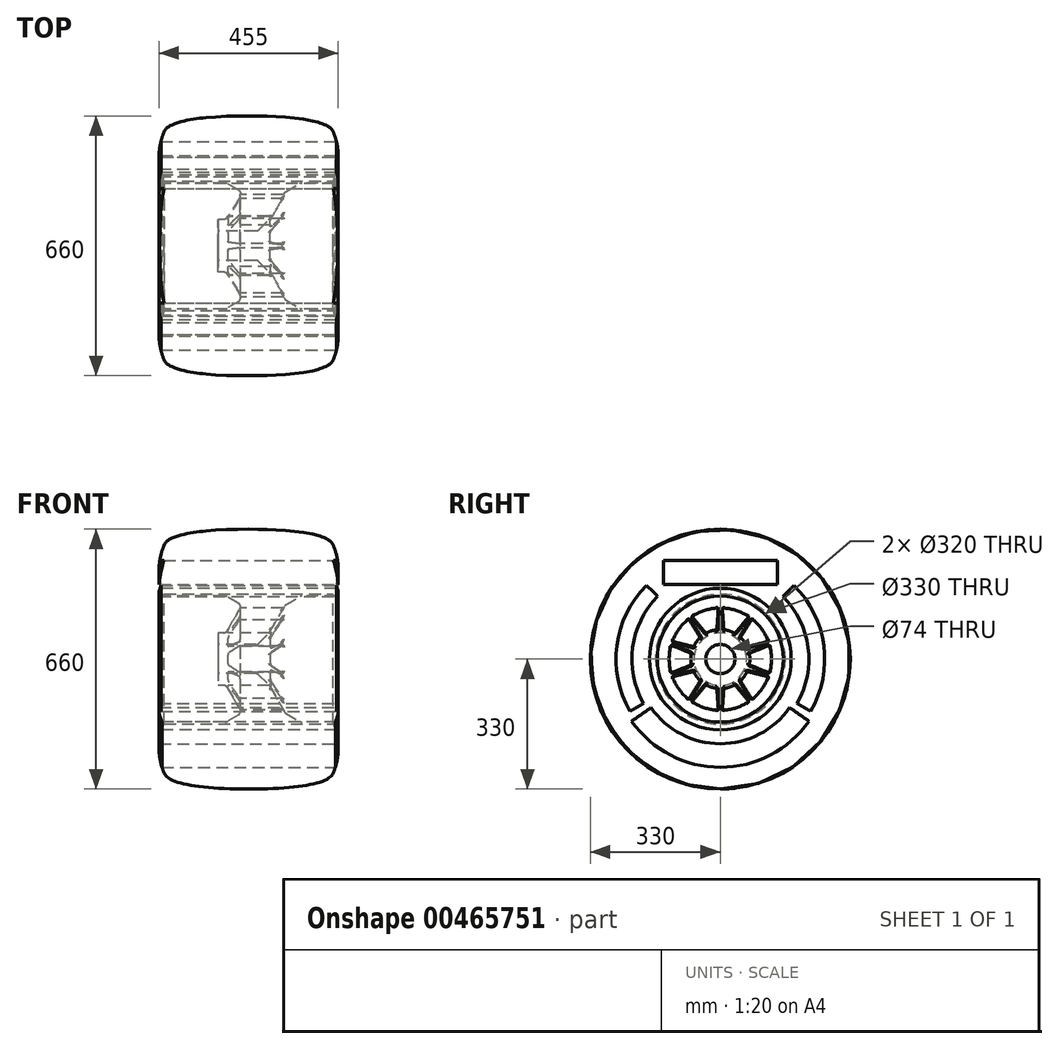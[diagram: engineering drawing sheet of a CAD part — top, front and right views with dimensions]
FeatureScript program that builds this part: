
annotation { "Feature Type Name" : "Feature", "Feature Type Description" : "" }
export const myFeature = defineFeature(function(context is Context, id is Id, definition is map)
    precondition{}
    {
        {
            var Q0;
            Q0=qCreatedBy(makeId("Front.planeOp"),FACE);
            var sketch = newSketch(context, id + "F0", { "sketchPlane" : qUnion([Q0])});
            skLineSegment(sketch, "E0.bottom", {"start": v(0, 0) * mm, "end": v(-232.5, 0) * mm, "construction": true});
            skLineSegment(sketch, "E0.top", {"start": v(0, 340) * mm, "end": v(-232.5, 340) * mm, "construction": true});
            skLineSegment(sketch, "E0.left", {"start": v(0, 0) * mm, "end": v(0, 340) * mm, "construction": true});
            skLineSegment(sketch, "E0.right", {"start": v(-232.5, 0) * mm, "end": v(-232.5, 340) * mm, "construction": true});
            skLineSegment(sketch, "E1", {"start": v(0, 165) * mm, "end": v(-214.65, 165) * mm});
            skEllipticalArc(sketch, "E2", {});
            skLineSegment(sketch, "E3", {"start": v(0, 330) * mm, "end": v(-232.5, 330) * mm, "construction": true});
            skLineSegment(sketch, "E4", {"start": v(-214.65, 165) * mm, "end": v(-214.65, 290) * mm, "construction": true});
            skEllipticalArc(sketch, "E5", {});
            skLineSegment(sketch, "E6", {"start": v(-227.5, 227.5) * mm, "end": v(-214.65, 227.5) * mm, "construction": true});
            skLineSegment(sketch, "E7.MirrorCS", {"start": v(0, 165) * mm, "end": v(214.65, 165) * mm});
            skEllipticalArc(sketch, "E8.MirrorCS", {});
            skEllipticalArc(sketch, "E9.MirrorCS", {});
            skLineSegment(sketch, "E10", {"start": v(-227.5, 227.5) * mm, "end": v(-227.5, 0) * mm, "construction": true});
            skLineSegment(sketch, "E11.MirrorCS", {"start": v(232.5, 0) * mm, "end": v(232.5, 340) * mm, "construction": true});
            skLineSegment(sketch, "E12.MirrorCS", {"start": v(0, 340) * mm, "end": v(232.5, 340) * mm, "construction": true});
            skLineSegment(sketch, "E13.MirrorCS", {"start": v(0, 0) * mm, "end": v(232.5, 0) * mm, "construction": true});
            const initialGuessF0  = {"E2": [0.9663548736200733, 0.07278752318222956, 0.9840924206940259, -0.17765727548449584, 1.201246100909484, 0.14589798289999634, 2.549372753708736, 3.1145633278998273], "E5": [0.08535, 0.2275, -1, 0, 0.31285, 0.22033704343395144, 5.995580380133269, 0.28760492704630874], "E8.MirrorCS": [-0.08535, 0.2275, 1, 0, 0.31285, 0.22033704343395144, 5.995580380133277, 0.28760492704631696], "E9.MirrorCS": [-0.9663548736200733, 0.07278752318222961, -0.984092420694026, -0.17765727548449584, 1.201246100909484, 0.14589798289999634, 3.168621979279758, 3.733812553470848]};
            skSetInitialGuess(sketch, initialGuessF0);
            skSolve(sketch);
        }
        {
            var Q0;
            Q0=qCreatedBy(makeId("Right.planeOp"),FACE);
            var sketch = newSketch(context, id + "F1", { "sketchPlane" : qUnion([Q0])});
            skLineSegment(sketch, "E14", {"start": v(0, 190) * mm, "end": v(0, -215) * mm, "construction": true});
            skLineSegment(sketch, "E15.bottom", {"start": v(0, 190) * mm, "end": v(-145, 190) * mm});
            skLineSegment(sketch, "E15.top", {"start": v(0, 250) * mm, "end": v(-145, 250) * mm});
            skLineSegment(sketch, "E15.left", {"start": v(0, 190) * mm, "end": v(0, 250) * mm});
            skLineSegment(sketch, "E15.right", {"start": v(-145, 190) * mm, "end": v(-145, 250) * mm});
            skArc(sketch, "E16", {"start": v(-159.1, 159.1) * mm, "mid": v(-223.08, 29.37) * mm, "end": v(-194.86, -112.5) * mm});
            skArc(sketch, "E17", {"start": v(-187.38, 187.38) * mm, "mid": v(-262.73, 34.59) * mm, "end": v(-229.5, -132.5) * mm});
            skLineSegment(sketch, "E18", {"start": v(-159.1, 159.1) * mm, "end": v(-187.38, 187.38) * mm});
            skLineSegment(sketch, "E19", {"start": v(-194.86, -112.5) * mm, "end": v(-229.5, -132.5) * mm});
            skArc(sketch, "E20", {"start": v(-176.12, -123.32) * mm, "mid": v(-99.28, -190.7) * mm, "end": v(0, -215) * mm});
            skArc(sketch, "E21", {"start": v(-225.27, -157.73) * mm, "mid": v(-126.98, -243.93) * mm, "end": v(0, -275) * mm});
            skLineSegment(sketch, "E22", {"start": v(-176.12, -123.32) * mm, "end": v(-225.27, -157.73) * mm});
            skLineSegment(sketch, "E23", {"start": v(0, -215) * mm, "end": v(0, -275) * mm});
            skLineSegment(sketch, "E24.MirrorCS", {"start": v(0, 250) * mm, "end": v(145, 250) * mm});
            skLineSegment(sketch, "E25.MirrorCS", {"start": v(145, 190) * mm, "end": v(145, 250) * mm});
            skLineSegment(sketch, "E26.MirrorCS", {"start": v(0, 190) * mm, "end": v(145, 190) * mm});
            skLineSegment(sketch, "E27.MirrorCS", {"start": v(159.1, 159.1) * mm, "end": v(187.38, 187.38) * mm});
            skArc(sketch, "E28.MirrorCS", {"start": v(187.38, 187.38) * mm, "mid": v(262.73, 34.59) * mm, "end": v(229.5, -132.5) * mm});
            skArc(sketch, "E29.MirrorCS", {"start": v(159.1, 159.1) * mm, "mid": v(223.08, 29.37) * mm, "end": v(194.86, -112.5) * mm});
            skLineSegment(sketch, "E30.MirrorCS", {"start": v(194.86, -112.5) * mm, "end": v(229.5, -132.5) * mm});
            skLineSegment(sketch, "E31.MirrorCS", {"start": v(176.12, -123.32) * mm, "end": v(225.27, -157.73) * mm});
            skArc(sketch, "E32.MirrorCS", {"start": v(225.27, -157.73) * mm, "mid": v(126.98, -243.93) * mm, "end": v(0, -275) * mm});
            skArc(sketch, "E33.MirrorCS", {"start": v(176.12, -123.32) * mm, "mid": v(99.28, -190.7) * mm, "end": v(0, -215) * mm});
            skSolve(sketch);
        }
        {
            var Q0;
            Q0=qCreatedBy(makeId("Front.planeOp"),FACE);
            var sketch = newSketch(context, id + "F2", { "sketchPlane" : qUnion([Q0])});
            skLineSegment(sketch, "E34.bottom", {"start": v(-222.5, 180) * mm, "end": v(222.5, 180) * mm});
            skLineSegment(sketch, "E34.top", {"start": v(-222.5, 160) * mm, "end": v(-60.18, 160) * mm});
            skLineSegment(sketch, "E34.left", {"start": v(-227.5, 175) * mm, "end": v(-227.5, 165) * mm});
            skLineSegment(sketch, "E34.right", {"start": v(227.5, 175) * mm, "end": v(227.5, 165) * mm});
            skPoint(sketch, "E35.visualSharp", {"position": v(-227.5, 160) * mm});
            skArc(sketch, "E35.filletArc", {"start": v(-227.5, 165) * mm, "mid": v(-226.04, 161.46) * mm, "end": v(-222.5, 160) * mm});
            skPoint(sketch, "E36.visualSharp", {"position": v(227.5, 160) * mm});
            skArc(sketch, "E36.filletArc", {"start": v(222.5, 160) * mm, "mid": v(226.04, 161.46) * mm, "end": v(227.5, 165) * mm});
            skPoint(sketch, "E37.visualSharp", {"position": v(227.5, 180) * mm});
            skArc(sketch, "E37.filletArc", {"start": v(227.5, 175) * mm, "mid": v(226.04, 178.54) * mm, "end": v(222.5, 180) * mm});
            skPoint(sketch, "E38.visualSharp", {"position": v(-227.5, 180) * mm});
            skArc(sketch, "E38.filletArc", {"start": v(-222.5, 180) * mm, "mid": v(-226.04, 178.54) * mm, "end": v(-227.5, 175) * mm});
            skLineSegment(sketch, "E39", {"start": v(18.36, 37) * mm, "end": v(-77.5, 37) * mm});
            skLineSegment(sketch, "E40", {"start": v(-77.5, 37) * mm, "end": v(-77.5, 67) * mm});
            skLineSegment(sketch, "E41", {"start": v(-77.5, 67) * mm, "end": v(-63.27, 67) * mm});
            skLineSegment(sketch, "E42", {"start": v(-54.61, 72) * mm, "end": v(-22.23, 128.09) * mm});
            skLineSegment(sketch, "E43", {"start": v(-25.9, 141.75) * mm, "end": v(-55.18, 158.66) * mm});
            skLineSegment(sketch, "E44", {"start": v(25.43, 39.93) * mm, "end": v(51.57, 66.07) * mm});
            skLineSegment(sketch, "E45", {"start": v(53.16, 68.14) * mm, "end": v(91.43, 134.43) * mm});
            skLineSegment(sketch, "E46", {"start": v(95.1, 138.09) * mm, "end": v(130.72, 158.66) * mm});
            skLineSegment(sketch, "E47.trimOffspring", {"start": v(135.72, 160) * mm, "end": v(222.5, 160) * mm});
            skPoint(sketch, "E48.visualSharp", {"position": v(-57.5, 160) * mm});
            skArc(sketch, "E48.filletArc", {"start": v(-55.18, 158.66) * mm, "mid": v(-57.6, 159.66) * mm, "end": v(-60.18, 160) * mm});
            skPoint(sketch, "E49.visualSharp", {"position": v(-57.5, 67) * mm});
            skArc(sketch, "E49.filletArc", {"start": v(-63.27, 67) * mm, "mid": v(-58.27, 68.34) * mm, "end": v(-54.61, 72) * mm});
            skPoint(sketch, "E50.visualSharp", {"position": v(22.5, 37) * mm});
            skArc(sketch, "E50.filletArc", {"start": v(18.36, 37) * mm, "mid": v(22.18, 37.76) * mm, "end": v(25.43, 39.93) * mm});
            skPoint(sketch, "E51.visualSharp", {"position": v(52.5, 67) * mm});
            skArc(sketch, "E51.filletArc", {"start": v(51.57, 66.07) * mm, "mid": v(52.43, 67.05) * mm, "end": v(53.16, 68.14) * mm});
            skPoint(sketch, "E52.visualSharp", {"position": v(92.77, 136.75) * mm});
            skPoint(sketch, "E53.visualSharp", {"position": v(133.04, 160) * mm});
            skArc(sketch, "E53.filletArc", {"start": v(135.72, 160) * mm, "mid": v(133.13, 159.66) * mm, "end": v(130.72, 158.66) * mm});
            skPoint(sketch, "E54.visualSharp", {"position": v(-17.23, 136.75) * mm});
            skArc(sketch, "E54.filletArc", {"start": v(-22.23, 128.09) * mm, "mid": v(-21.23, 135.68) * mm, "end": v(-25.9, 141.75) * mm});
            skArc(sketch, "E55.filletArc", {"start": v(95.1, 138.09) * mm, "mid": v(93.02, 136.5) * mm, "end": v(91.43, 134.43) * mm});
            skSolve(sketch);
        }
        {
            var Q0;
            Q0=qCreatedBy(makeId("Right.planeOp"),FACE);
            var sketch = newSketch(context, id + "F3", { "sketchPlane" : qUnion([Q0])});
            skLineSegment(sketch, "E56", {"start": v(5.4, 124.22) * mm, "end": v(8.6, 78.49) * mm});
            skLineSegment(sketch, "E57", {"start": v(40.17, 123.64) * mm, "end": v(23.18, 71.33) * mm, "construction": true});
            skLineSegment(sketch, "E58", {"start": v(23.18, 71.33) * mm, "end": v(0, 0) * mm, "construction": true});
            skArc(sketch, "E59", {"start": v(23.18, 71.33) * mm, "mid": v(18, 72.8) * mm, "end": v(12.73, 73.91) * mm});
            skArc(sketch, "E60", {"start": v(40.17, 123.64) * mm, "mid": v(25.66, 127.44) * mm, "end": v(10.8, 129.55) * mm});
            skArc(sketch, "E61.MirrorCS", {"start": v(23.18, 71.33) * mm, "mid": v(28.23, 69.48) * mm, "end": v(33.14, 67.28) * mm});
            skLineSegment(sketch, "E62.MirrorCS", {"start": v(68.65, 103.67) * mm, "end": v(39.18, 68.55) * mm});
            skArc(sketch, "E63.MirrorCS", {"start": v(40.17, 123.64) * mm, "mid": v(54.15, 118.18) * mm, "end": v(67.4, 111.16) * mm});
            skPoint(sketch, "E64.visualSharp", {"position": v(8.88, 74.47) * mm});
            skArc(sketch, "E64.filletArc", {"start": v(8.6, 78.49) * mm, "mid": v(9.87, 75.49) * mm, "end": v(12.73, 73.91) * mm});
            skPoint(sketch, "E65.visualSharp", {"position": v(5, 129.9) * mm});
            skArc(sketch, "E65.filletArc", {"start": v(10.8, 129.55) * mm, "mid": v(6.87, 128.13) * mm, "end": v(5.4, 124.22) * mm});
            skPoint(sketch, "E66.visualSharp", {"position": v(36.6, 65.47) * mm});
            skArc(sketch, "E66.filletArc", {"start": v(33.14, 67.28) * mm, "mid": v(36.38, 66.87) * mm, "end": v(39.18, 68.55) * mm});
            skPoint(sketch, "E67.visualSharp", {"position": v(72.31, 108.03) * mm});
            skArc(sketch, "E67.filletArc", {"start": v(68.65, 103.67) * mm, "mid": v(69.75, 107.7) * mm, "end": v(67.4, 111.16) * mm});
            skLineSegment(sketch, "E68.1.0", {"start": v(-5.4, 124.22) * mm, "end": v(-8.6, 78.49) * mm});
            skArc(sketch, "E68.1.1", {"start": v(-5.4, 124.22) * mm, "mid": v(-6.87, 128.13) * mm, "end": v(-10.8, 129.55) * mm});
            skArc(sketch, "E68.1.2", {"start": v(-40.17, 123.64) * mm, "mid": v(-25.66, 127.44) * mm, "end": v(-10.8, 129.55) * mm});
            skArc(sketch, "E68.1.3", {"start": v(-40.17, 123.64) * mm, "mid": v(-54.15, 118.18) * mm, "end": v(-67.4, 111.16) * mm});
            skArc(sketch, "E68.1.4", {"start": v(-67.4, 111.16) * mm, "mid": v(-69.75, 107.7) * mm, "end": v(-68.65, 103.67) * mm});
            skLineSegment(sketch, "E68.1.5", {"start": v(-68.65, 103.67) * mm, "end": v(-39.18, 68.55) * mm});
            skArc(sketch, "E68.1.6", {"start": v(-39.18, 68.55) * mm, "mid": v(-36.38, 66.87) * mm, "end": v(-33.14, 67.28) * mm});
            skArc(sketch, "E68.1.7", {"start": v(-23.18, 71.33) * mm, "mid": v(-28.23, 69.48) * mm, "end": v(-33.14, 67.28) * mm});
            skArc(sketch, "E68.1.8", {"start": v(-23.18, 71.33) * mm, "mid": v(-18, 72.8) * mm, "end": v(-12.73, 73.91) * mm});
            skArc(sketch, "E68.1.9", {"start": v(-12.73, 73.91) * mm, "mid": v(-9.87, 75.49) * mm, "end": v(-8.6, 78.49) * mm});
            skLineSegment(sketch, "E68.2.0", {"start": v(-77.38, 97.32) * mm, "end": v(-53.09, 58.45) * mm});
            skArc(sketch, "E68.2.1", {"start": v(-77.38, 97.32) * mm, "mid": v(-80.87, 99.62) * mm, "end": v(-84.89, 98.46) * mm});
            skArc(sketch, "E68.2.2", {"start": v(-105.17, 76.41) * mm, "mid": v(-95.67, 88.02) * mm, "end": v(-84.89, 98.46) * mm});
            skArc(sketch, "E68.2.3", {"start": v(-105.17, 76.41) * mm, "mid": v(-113.28, 63.78) * mm, "end": v(-119.87, 50.3) * mm});
            skArc(sketch, "E68.2.4", {"start": v(-119.87, 50.3) * mm, "mid": v(-119.73, 46.13) * mm, "end": v(-116.47, 43.52) * mm});
            skLineSegment(sketch, "E68.2.5", {"start": v(-116.47, 43.52) * mm, "end": v(-72, 32.43) * mm});
            skArc(sketch, "E68.2.6", {"start": v(-72, 32.43) * mm, "mid": v(-68.74, 32.72) * mm, "end": v(-66.36, 34.95) * mm});
            skArc(sketch, "E68.2.7", {"start": v(-60.68, 44.08) * mm, "mid": v(-63.68, 39.62) * mm, "end": v(-66.36, 34.95) * mm});
            skArc(sketch, "E68.2.8", {"start": v(-60.68, 44.08) * mm, "mid": v(-57.36, 48.32) * mm, "end": v(-53.75, 52.31) * mm});
            skArc(sketch, "E68.2.9", {"start": v(-53.75, 52.31) * mm, "mid": v(-52.36, 55.27) * mm, "end": v(-53.09, 58.45) * mm});
            skLineSegment(sketch, "E68.3.0", {"start": v(-119.8, 33.25) * mm, "end": v(-77.3, 16.08) * mm});
            skArc(sketch, "E68.3.1", {"start": v(-119.8, 33.25) * mm, "mid": v(-123.98, 33.06) * mm, "end": v(-126.55, 29.76) * mm});
            skArc(sketch, "E68.3.2", {"start": v(-130, 0) * mm, "mid": v(-129.13, 14.98) * mm, "end": v(-126.55, 29.76) * mm});
            skArc(sketch, "E68.3.3", {"start": v(-130, 0) * mm, "mid": v(-129.13, -14.98) * mm, "end": v(-126.55, -29.76) * mm});
            skArc(sketch, "E68.3.4", {"start": v(-126.55, -29.76) * mm, "mid": v(-123.98, -33.06) * mm, "end": v(-119.8, -33.25) * mm});
            skLineSegment(sketch, "E68.3.5", {"start": v(-119.8, -33.25) * mm, "end": v(-77.3, -16.08) * mm});
            skArc(sketch, "E68.3.6", {"start": v(-77.3, -16.08) * mm, "mid": v(-74.84, -13.94) * mm, "end": v(-74.23, -10.73) * mm});
            skArc(sketch, "E68.3.7", {"start": v(-75, 0) * mm, "mid": v(-74.8, -5.38) * mm, "end": v(-74.23, -10.73) * mm});
            skArc(sketch, "E68.3.8", {"start": v(-75, 0) * mm, "mid": v(-74.8, 5.38) * mm, "end": v(-74.23, 10.73) * mm});
            skArc(sketch, "E68.3.9", {"start": v(-74.23, 10.73) * mm, "mid": v(-74.84, 13.94) * mm, "end": v(-77.3, 16.08) * mm});
            skLineSegment(sketch, "E68.4.0", {"start": v(-116.47, -43.52) * mm, "end": v(-72, -32.43) * mm});
            skArc(sketch, "E68.4.1", {"start": v(-116.47, -43.52) * mm, "mid": v(-119.73, -46.13) * mm, "end": v(-119.87, -50.3) * mm});
            skArc(sketch, "E68.4.2", {"start": v(-105.17, -76.41) * mm, "mid": v(-113.28, -63.78) * mm, "end": v(-119.87, -50.3) * mm});
            skArc(sketch, "E68.4.3", {"start": v(-105.17, -76.41) * mm, "mid": v(-95.67, -88.02) * mm, "end": v(-84.89, -98.46) * mm});
            skArc(sketch, "E68.4.4", {"start": v(-84.89, -98.46) * mm, "mid": v(-80.87, -99.62) * mm, "end": v(-77.38, -97.32) * mm});
            skLineSegment(sketch, "E68.4.5", {"start": v(-77.38, -97.32) * mm, "end": v(-53.09, -58.45) * mm});
            skArc(sketch, "E68.4.6", {"start": v(-53.09, -58.45) * mm, "mid": v(-52.36, -55.27) * mm, "end": v(-53.75, -52.31) * mm});
            skArc(sketch, "E68.4.7", {"start": v(-60.68, -44.08) * mm, "mid": v(-57.36, -48.32) * mm, "end": v(-53.75, -52.31) * mm});
            skArc(sketch, "E68.4.8", {"start": v(-60.68, -44.08) * mm, "mid": v(-63.68, -39.62) * mm, "end": v(-66.36, -34.95) * mm});
            skArc(sketch, "E68.4.9", {"start": v(-66.36, -34.95) * mm, "mid": v(-68.74, -32.72) * mm, "end": v(-72, -32.43) * mm});
            skLineSegment(sketch, "E68.5.0", {"start": v(-68.65, -103.67) * mm, "end": v(-39.18, -68.55) * mm});
            skArc(sketch, "E68.5.1", {"start": v(-68.65, -103.67) * mm, "mid": v(-69.75, -107.7) * mm, "end": v(-67.4, -111.16) * mm});
            skArc(sketch, "E68.5.2", {"start": v(-40.17, -123.64) * mm, "mid": v(-54.15, -118.18) * mm, "end": v(-67.4, -111.16) * mm});
            skArc(sketch, "E68.5.3", {"start": v(-40.17, -123.64) * mm, "mid": v(-25.66, -127.44) * mm, "end": v(-10.8, -129.55) * mm});
            skArc(sketch, "E68.5.4", {"start": v(-10.8, -129.55) * mm, "mid": v(-6.87, -128.13) * mm, "end": v(-5.4, -124.22) * mm});
            skLineSegment(sketch, "E68.5.5", {"start": v(-5.4, -124.22) * mm, "end": v(-8.6, -78.49) * mm});
            skArc(sketch, "E68.5.6", {"start": v(-8.6, -78.49) * mm, "mid": v(-9.87, -75.49) * mm, "end": v(-12.73, -73.91) * mm});
            skArc(sketch, "E68.5.7", {"start": v(-23.18, -71.33) * mm, "mid": v(-18, -72.8) * mm, "end": v(-12.73, -73.91) * mm});
            skArc(sketch, "E68.5.8", {"start": v(-23.18, -71.33) * mm, "mid": v(-28.23, -69.48) * mm, "end": v(-33.14, -67.28) * mm});
            skArc(sketch, "E68.5.9", {"start": v(-33.14, -67.28) * mm, "mid": v(-36.38, -66.87) * mm, "end": v(-39.18, -68.55) * mm});
            skLineSegment(sketch, "E68.6.0", {"start": v(5.4, -124.22) * mm, "end": v(8.6, -78.49) * mm});
            skArc(sketch, "E68.6.1", {"start": v(5.4, -124.22) * mm, "mid": v(6.87, -128.13) * mm, "end": v(10.8, -129.55) * mm});
            skArc(sketch, "E68.6.2", {"start": v(40.17, -123.64) * mm, "mid": v(25.66, -127.44) * mm, "end": v(10.8, -129.55) * mm});
            skArc(sketch, "E68.6.3", {"start": v(40.17, -123.64) * mm, "mid": v(54.15, -118.18) * mm, "end": v(67.4, -111.16) * mm});
            skArc(sketch, "E68.6.4", {"start": v(67.4, -111.16) * mm, "mid": v(69.75, -107.7) * mm, "end": v(68.65, -103.67) * mm});
            skLineSegment(sketch, "E68.6.5", {"start": v(68.65, -103.67) * mm, "end": v(39.18, -68.55) * mm});
            skArc(sketch, "E68.6.6", {"start": v(39.18, -68.55) * mm, "mid": v(36.38, -66.87) * mm, "end": v(33.14, -67.28) * mm});
            skArc(sketch, "E68.6.7", {"start": v(23.18, -71.33) * mm, "mid": v(28.23, -69.48) * mm, "end": v(33.14, -67.28) * mm});
            skArc(sketch, "E68.6.8", {"start": v(23.18, -71.33) * mm, "mid": v(18, -72.8) * mm, "end": v(12.73, -73.91) * mm});
            skArc(sketch, "E68.6.9", {"start": v(12.73, -73.91) * mm, "mid": v(9.87, -75.49) * mm, "end": v(8.6, -78.49) * mm});
            skLineSegment(sketch, "E68.7.0", {"start": v(77.38, -97.32) * mm, "end": v(53.09, -58.45) * mm});
            skArc(sketch, "E68.7.1", {"start": v(77.38, -97.32) * mm, "mid": v(80.87, -99.62) * mm, "end": v(84.89, -98.46) * mm});
            skArc(sketch, "E68.7.2", {"start": v(105.17, -76.41) * mm, "mid": v(95.67, -88.02) * mm, "end": v(84.89, -98.46) * mm});
            skArc(sketch, "E68.7.3", {"start": v(105.17, -76.41) * mm, "mid": v(113.28, -63.78) * mm, "end": v(119.87, -50.3) * mm});
            skArc(sketch, "E68.7.4", {"start": v(119.87, -50.3) * mm, "mid": v(119.73, -46.13) * mm, "end": v(116.47, -43.52) * mm});
            skLineSegment(sketch, "E68.7.5", {"start": v(116.47, -43.52) * mm, "end": v(72, -32.43) * mm});
            skArc(sketch, "E68.7.6", {"start": v(72, -32.43) * mm, "mid": v(68.74, -32.72) * mm, "end": v(66.36, -34.95) * mm});
            skArc(sketch, "E68.7.7", {"start": v(60.68, -44.08) * mm, "mid": v(63.68, -39.62) * mm, "end": v(66.36, -34.95) * mm});
            skArc(sketch, "E68.7.8", {"start": v(60.68, -44.08) * mm, "mid": v(57.36, -48.32) * mm, "end": v(53.75, -52.31) * mm});
            skArc(sketch, "E68.7.9", {"start": v(53.75, -52.31) * mm, "mid": v(52.36, -55.27) * mm, "end": v(53.09, -58.45) * mm});
            skLineSegment(sketch, "E68.8.0", {"start": v(119.8, -33.25) * mm, "end": v(77.3, -16.08) * mm});
            skArc(sketch, "E68.8.1", {"start": v(119.8, -33.25) * mm, "mid": v(123.98, -33.06) * mm, "end": v(126.55, -29.76) * mm});
            skArc(sketch, "E68.8.2", {"start": v(130, 0) * mm, "mid": v(129.13, -14.98) * mm, "end": v(126.55, -29.76) * mm});
            skArc(sketch, "E68.8.3", {"start": v(130, 0) * mm, "mid": v(129.13, 14.98) * mm, "end": v(126.55, 29.76) * mm});
            skArc(sketch, "E68.8.4", {"start": v(126.55, 29.76) * mm, "mid": v(123.98, 33.06) * mm, "end": v(119.8, 33.25) * mm});
            skLineSegment(sketch, "E68.8.5", {"start": v(119.8, 33.25) * mm, "end": v(77.3, 16.08) * mm});
            skArc(sketch, "E68.8.6", {"start": v(77.3, 16.08) * mm, "mid": v(74.84, 13.94) * mm, "end": v(74.23, 10.73) * mm});
            skArc(sketch, "E68.8.7", {"start": v(75, 0) * mm, "mid": v(74.8, 5.38) * mm, "end": v(74.23, 10.73) * mm});
            skArc(sketch, "E68.8.8", {"start": v(75, 0) * mm, "mid": v(74.8, -5.38) * mm, "end": v(74.23, -10.73) * mm});
            skArc(sketch, "E68.8.9", {"start": v(74.23, -10.73) * mm, "mid": v(74.84, -13.94) * mm, "end": v(77.3, -16.08) * mm});
            skLineSegment(sketch, "E68.9.0", {"start": v(116.47, 43.52) * mm, "end": v(72, 32.43) * mm});
            skArc(sketch, "E68.9.1", {"start": v(116.47, 43.52) * mm, "mid": v(119.73, 46.13) * mm, "end": v(119.87, 50.3) * mm});
            skArc(sketch, "E68.9.2", {"start": v(105.17, 76.41) * mm, "mid": v(113.28, 63.78) * mm, "end": v(119.87, 50.3) * mm});
            skArc(sketch, "E68.9.3", {"start": v(105.17, 76.41) * mm, "mid": v(95.67, 88.02) * mm, "end": v(84.89, 98.46) * mm});
            skArc(sketch, "E68.9.4", {"start": v(84.89, 98.46) * mm, "mid": v(80.87, 99.62) * mm, "end": v(77.38, 97.32) * mm});
            skLineSegment(sketch, "E68.9.5", {"start": v(77.38, 97.32) * mm, "end": v(53.09, 58.45) * mm});
            skArc(sketch, "E68.9.6", {"start": v(53.09, 58.45) * mm, "mid": v(52.36, 55.27) * mm, "end": v(53.75, 52.31) * mm});
            skArc(sketch, "E68.9.7", {"start": v(60.68, 44.08) * mm, "mid": v(57.36, 48.32) * mm, "end": v(53.75, 52.31) * mm});
            skArc(sketch, "E68.9.8", {"start": v(60.68, 44.08) * mm, "mid": v(63.68, 39.62) * mm, "end": v(66.36, 34.95) * mm});
            skArc(sketch, "E68.9.9", {"start": v(66.36, 34.95) * mm, "mid": v(68.74, 32.72) * mm, "end": v(72, 32.43) * mm});
            skSolve(sketch);
        }
        {
            var Q0;
            Q0=makeQuery(id+"F0.imprint","IMPRINT",FACE,{"disambiguationData":[TD([[makeQuery(id+"F0.imprint","IMPRINT",EDGE,{"derivedFrom":sQuery(id+"F0.wireOp",EDGE,"E1")}),-1.0]])]});
            var Q1;
            Q1=sQuery(id+"F0.wireOp",EDGE,"E0.bottom");
            revolve(context, id + "F4", {"entities" : qUnion([Q0]), "axis" : qUnion([Q1]), "revolveType" : RevolveType.FULL});
        }
        {
            var Q0;
            Q0=qSketchRegion(id+"F1",true);
            var Q1;
            Q1=makeQuery(id+"F4.opRevolve","SWEPT_FACE",FACE,{"disambiguationData":[OSD([sQuery(id+"F0.wireOp",EDGE,"E5")])]});
            extrude(context, id + "F5", {"entities" : qUnion([Q0]), "endBound" : BoundingType.UP_TO_NEXT, "oppositeDirection" : true, "depth" : 25 * mm, "hasSecondDirection" : true, "secondDirectionBound" : BoundingType.UP_TO_NEXT, "secondDirectionOppositeDirection" : false, "secondDirectionBoundEntityFace" : qUnion([Q1]), "secondDirectionDepth" : 25 * mm});
        }
        {
            var Q0;
            Q0=makeQuery(id+"F5.opExtrude","SWEPT_BODY",BODY,{"disambiguationData":[OSD([sQuery(id+"F1.wireOp",EDGE,"E15.bottom"),sQuery(id+"F1.wireOp",EDGE,"E15.top"),sQuery(id+"F1.wireOp",EDGE,"E15.right"),sQuery(id+"F1.wireOp",EDGE,"E24.MirrorCS"),sQuery(id+"F1.wireOp",EDGE,"E25.MirrorCS"),sQuery(id+"F1.wireOp",EDGE,"E26.MirrorCS")])]});
            var Q1;
            Q1=makeQuery(id+"F5.opExtrude","SWEPT_BODY",BODY,{"disambiguationData":[OSD([sQuery(id+"F1.wireOp",EDGE,"E27.MirrorCS"),sQuery(id+"F1.wireOp",EDGE,"E28.MirrorCS"),sQuery(id+"F1.wireOp",EDGE,"E29.MirrorCS"),sQuery(id+"F1.wireOp",EDGE,"E30.MirrorCS")])]});
            var Q2;
            Q2=makeQuery(id+"F5.opExtrude","SWEPT_BODY",BODY,{"disambiguationData":[OSD([sQuery(id+"F1.wireOp",EDGE,"E20"),sQuery(id+"F1.wireOp",EDGE,"E21"),sQuery(id+"F1.wireOp",EDGE,"E22"),sQuery(id+"F1.wireOp",EDGE,"E31.MirrorCS"),sQuery(id+"F1.wireOp",EDGE,"E32.MirrorCS"),sQuery(id+"F1.wireOp",EDGE,"E33.MirrorCS")])]});
            var Q3;
            Q3=makeQuery(id+"F5.opExtrude","SWEPT_BODY",BODY,{"disambiguationData":[OSD([sQuery(id+"F1.wireOp",EDGE,"E16"),sQuery(id+"F1.wireOp",EDGE,"E17"),sQuery(id+"F1.wireOp",EDGE,"E18"),sQuery(id+"F1.wireOp",EDGE,"E19")])]});
            var Q4;
            Q4=makeQuery(id+"F4.opRevolve","SWEPT_BODY",BODY,{"disambiguationData":[OSD([sQuery(id+"F0.wireOp",EDGE,"E1"),sQuery(id+"F0.wireOp",EDGE,"E2"),sQuery(id+"F0.wireOp",EDGE,"E5"),sQuery(id+"F0.wireOp",EDGE,"E7.MirrorCS"),sQuery(id+"F0.wireOp",EDGE,"E8.MirrorCS"),sQuery(id+"F0.wireOp",EDGE,"E9.MirrorCS")])]});
            booleanBodies(context, id + "F6", {"operationType" : BooleanOperationType.SUBTRACTION, "tools" : qUnion([Q0, Q1, Q2, Q3]), "targets" : qUnion([Q4]), "keepTools" : true});
        }
        {
            var Q0;
            Q0=qSketchRegion(id+"F2",true);
            var Q1;
            Q1=sQuery(id+"F0.wireOp",EDGE,"E13.MirrorCS");
            revolve(context, id + "F7", {"entities" : qUnion([Q0]), "axis" : qUnion([Q1]), "revolveType" : RevolveType.FULL});
        }
        {
            var Q0;
            Q0=qSketchRegion(id+"F3",true);
            extrude(context, id + "F8", {"entities" : qUnion([Q0]), "operationType" : NewBodyOperationType.REMOVE, "endBound" : BoundingType.THROUGH_ALL, "depth" : 25 * mm, "hasSecondDirection" : true, "secondDirectionBound" : BoundingType.THROUGH_ALL, "secondDirectionOppositeDirection" : true, "secondDirectionDepth" : 25 * mm});
        }
        {
            var Q0;
            Q0=makeQuery(id+"F8.boolean.opBoolean","INTERSECT",EDGE,{"derivedFrom":[makeQuery(id+"F7.opRevolve","SWEPT_FACE",FACE,{"disambiguationData":[OSD([sQuery(id+"F2.wireOp",EDGE,"E45")])]}),makeQuery(id+"F8.opExtrude","SWEPT_FACE",FACE,{"disambiguationData":[OSD([sQuery(id+"F3.wireOp",EDGE,"E68.1.5")])]})]});
            var Q1;
            Q1=makeQuery(id+"F8.boolean.opBoolean","INTERSECT",EDGE,{"derivedFrom":[makeQuery(id+"F7.opRevolve","SWEPT_FACE",FACE,{"disambiguationData":[OSD([sQuery(id+"F2.wireOp",EDGE,"E45")])]}),makeQuery(id+"F8.opExtrude","SWEPT_FACE",FACE,{"disambiguationData":[OSD([sQuery(id+"F3.wireOp",EDGE,"E56")])]})]});
            var Q2;
            Q2=makeQuery(id+"F8.boolean.opBoolean","INTERSECT",EDGE,{"derivedFrom":[makeQuery(id+"F7.opRevolve","SWEPT_FACE",FACE,{"disambiguationData":[OSD([sQuery(id+"F2.wireOp",EDGE,"E45")])]}),makeQuery(id+"F8.opExtrude","SWEPT_FACE",FACE,{"disambiguationData":[OSD([sQuery(id+"F3.wireOp",EDGE,"E68.9.5")])]})]});
            var Q3;
            Q3=makeQuery(id+"F8.boolean.opBoolean","INTERSECT",EDGE,{"derivedFrom":[makeQuery(id+"F7.opRevolve","SWEPT_FACE",FACE,{"disambiguationData":[OSD([sQuery(id+"F2.wireOp",EDGE,"E45")])]}),makeQuery(id+"F8.opExtrude","SWEPT_FACE",FACE,{"disambiguationData":[OSD([sQuery(id+"F3.wireOp",EDGE,"E68.8.5")])]})]});
            var Q4;
            Q4=makeQuery(id+"F8.boolean.opBoolean","INTERSECT",EDGE,{"derivedFrom":[makeQuery(id+"F7.opRevolve","SWEPT_FACE",FACE,{"disambiguationData":[OSD([sQuery(id+"F2.wireOp",EDGE,"E45")])]}),makeQuery(id+"F8.opExtrude","SWEPT_FACE",FACE,{"disambiguationData":[OSD([sQuery(id+"F3.wireOp",EDGE,"E68.7.5")])]})]});
            var Q5;
            Q5=makeQuery(id+"F8.boolean.opBoolean","INTERSECT",EDGE,{"derivedFrom":[makeQuery(id+"F7.opRevolve","SWEPT_FACE",FACE,{"disambiguationData":[OSD([sQuery(id+"F2.wireOp",EDGE,"E45")])]}),makeQuery(id+"F8.opExtrude","SWEPT_FACE",FACE,{"disambiguationData":[OSD([sQuery(id+"F3.wireOp",EDGE,"E68.6.5")])]})]});
            var Q6;
            Q6=makeQuery(id+"F8.boolean.opBoolean","INTERSECT",EDGE,{"derivedFrom":[makeQuery(id+"F7.opRevolve","SWEPT_FACE",FACE,{"disambiguationData":[OSD([sQuery(id+"F2.wireOp",EDGE,"E45")])]}),makeQuery(id+"F8.opExtrude","SWEPT_FACE",FACE,{"disambiguationData":[OSD([sQuery(id+"F3.wireOp",EDGE,"E68.5.5")])]})]});
            var Q7;
            Q7=makeQuery(id+"F8.boolean.opBoolean","INTERSECT",EDGE,{"derivedFrom":[makeQuery(id+"F7.opRevolve","SWEPT_FACE",FACE,{"disambiguationData":[OSD([sQuery(id+"F2.wireOp",EDGE,"E45")])]}),makeQuery(id+"F8.opExtrude","SWEPT_FACE",FACE,{"disambiguationData":[OSD([sQuery(id+"F3.wireOp",EDGE,"E68.4.5")])]})]});
            var Q8;
            Q8=makeQuery(id+"F8.boolean.opBoolean","INTERSECT",EDGE,{"derivedFrom":[makeQuery(id+"F7.opRevolve","SWEPT_FACE",FACE,{"disambiguationData":[OSD([sQuery(id+"F2.wireOp",EDGE,"E45")])]}),makeQuery(id+"F8.opExtrude","SWEPT_FACE",FACE,{"disambiguationData":[OSD([sQuery(id+"F3.wireOp",EDGE,"E68.3.5")])]})]});
            var Q9;
            Q9=makeQuery(id+"F8.boolean.opBoolean","INTERSECT",EDGE,{"derivedFrom":[makeQuery(id+"F7.opRevolve","SWEPT_FACE",FACE,{"disambiguationData":[OSD([sQuery(id+"F2.wireOp",EDGE,"E45")])]}),makeQuery(id+"F8.opExtrude","SWEPT_FACE",FACE,{"disambiguationData":[OSD([sQuery(id+"F3.wireOp",EDGE,"E68.2.5")])]})]});
            fillet(context, id + "F9", {"entities" : qUnion([Q0, Q1, Q2, Q3, Q4, Q5, Q6, Q7, Q8, Q9]), "radius" : 3 * mm, "tangentPropagation" : true, "allowEdgeOverflow" : false});
        }
    });
